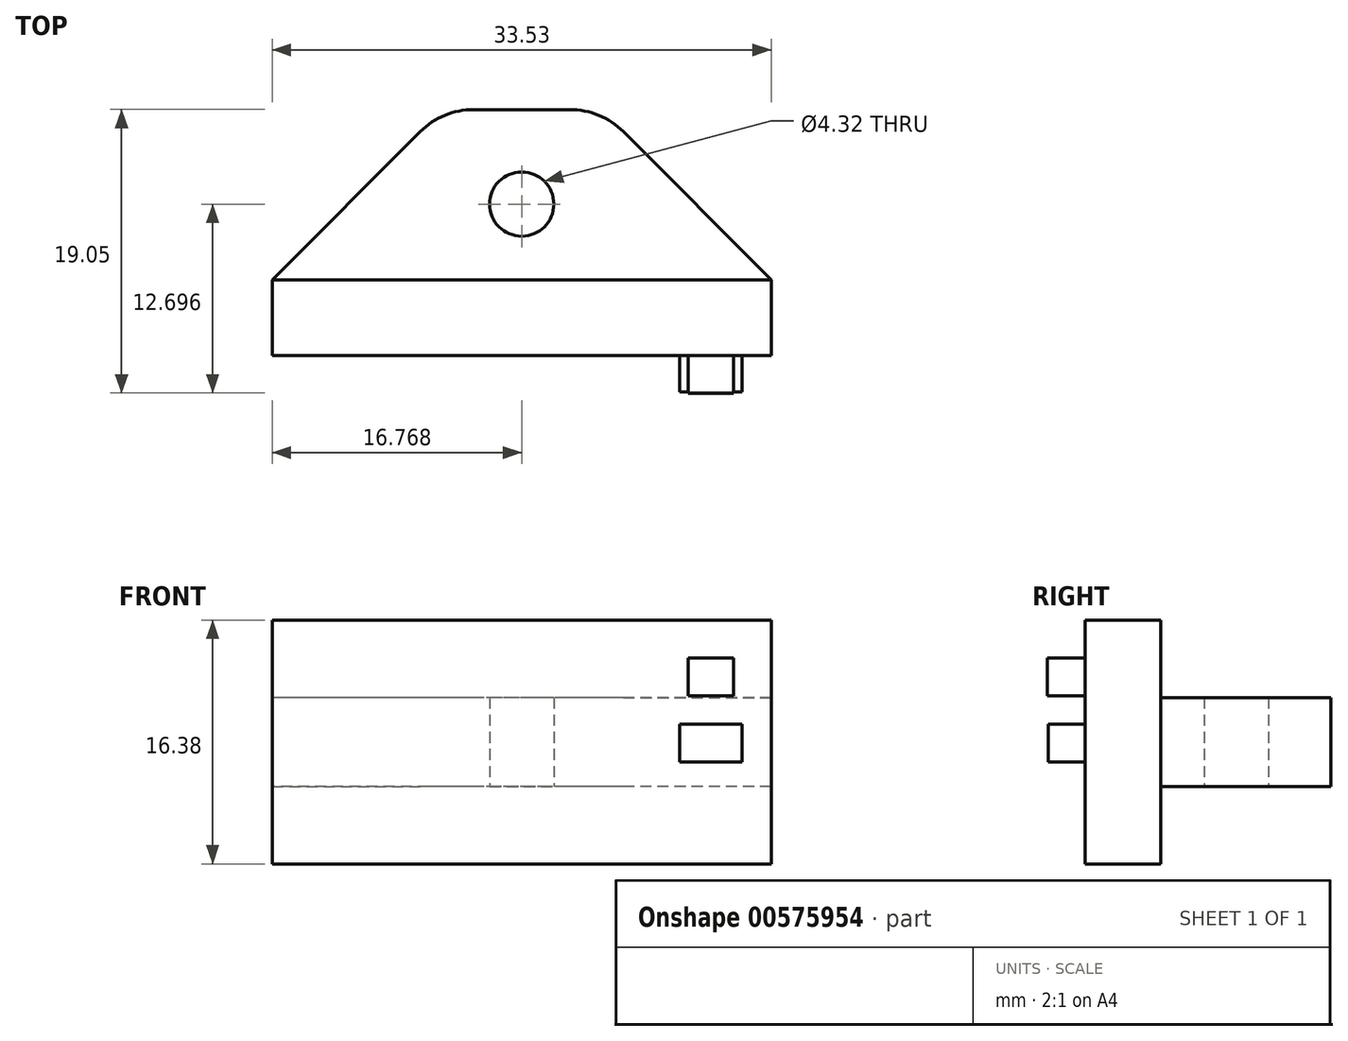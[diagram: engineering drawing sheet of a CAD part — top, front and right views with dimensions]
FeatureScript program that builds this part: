
annotation { "Feature Type Name" : "Feature", "Feature Type Description" : "" }
export const myFeature = defineFeature(function(context is Context, id is Id, definition is map)
    precondition{}
    {
        {
            var Q0;
            Q0=qCreatedBy(makeId("Top.planeOp"),FACE);
            var sketch = newSketch(context, id + "F0", { "sketchPlane" : qUnion([Q0])});
            skLineSegment(sketch, "E0.bottom", {"start": v(-12.43, 11) * mm, "end": v(21.1, 11) * mm});
            skLineSegment(sketch, "E0.top", {"start": v(-12.43, 5.92) * mm, "end": v(21.1, 5.92) * mm});
            skLineSegment(sketch, "E0.left", {"start": v(-12.43, 11) * mm, "end": v(-12.43, 5.92) * mm});
            skLineSegment(sketch, "E0.right", {"start": v(21.1, 11) * mm, "end": v(21.1, 5.92) * mm});
            skSolve(sketch);
        }
        {
            var Q0;
            Q0=makeQuery(id+"F0.imprint","IMPRINT",FACE,{"disambiguationData":[TD([[makeQuery(id+"F0.imprint","IMPRINT",EDGE,{"derivedFrom":sQuery(id+"F0.wireOp",EDGE,"E0.bottom")}),-1.0]])]});
            extrude(context, id + "F1", {"entities" : qUnion([Q0]), "depth" : 16.38 * mm, "offsetDistance" : 25.4 * mm});
        }
        {
            var Q0;
            Q0=makeQuery(id+"F1.opExtrude","SWEPT_FACE",FACE,{"disambiguationData":[OSD([sQuery(id+"F0.wireOp",EDGE,"E0.bottom")])]});
            var sketch = newSketch(context, id + "F2", { "sketchPlane" : qUnion([Q0])});
            skLineSegment(sketch, "E1.bottom", {"start": v(-21.1, 11.18) * mm, "end": v(12.43, 11.18) * mm});
            skLineSegment(sketch, "E1.top", {"start": v(-21.1, 5.2) * mm, "end": v(12.43, 5.2) * mm});
            skLineSegment(sketch, "E1.left", {"start": v(-21.1, 11.18) * mm, "end": v(-21.1, 5.2) * mm});
            skLineSegment(sketch, "E1.right", {"start": v(12.43, 11.18) * mm, "end": v(12.43, 5.2) * mm});
            skSolve(sketch);
        }
        {
            var Q0;
            Q0=makeQuery(id+"F2.imprint","IMPRINT",FACE,{"disambiguationData":[TD([[makeQuery(id+"F2.imprint","IMPRINT",EDGE,{"derivedFrom":sQuery(id+"F2.wireOp",EDGE,"E1.bottom")}),-1.0]])]});
            extrude(context, id + "F3", {"entities" : qUnion([Q0]), "operationType" : NewBodyOperationType.ADD, "depth" : 11.43 * mm, "offsetDistance" : 25.4 * mm});
        }
        {
            var Q0;
            Q0=makeQuery(id+"F3.opExtrude","CAP_EDGE",EDGE,{"disambiguationData":[OSD([sQuery(id+"F2.wireOp",EDGE,"E1.right")])],"isStart":false});
            var Q1;
            Q1=makeQuery(id+"F3.opExtrude","CAP_EDGE",EDGE,{"disambiguationData":[OSD([sQuery(id+"F2.wireOp",EDGE,"E1.left")])],"isStart":false});
            chamfer(context, id + "F4", {"entities" : qUnion([Q0, Q1]), "width" : 11.43 * mm, "tangentPropagation" : true});
        }
        {
            var Q0;
            Q0=makeQuery(id+"F3.opExtrude","SWEPT_FACE",FACE,{"disambiguationData":[OSD([sQuery(id+"F2.wireOp",EDGE,"E1.top")])]});
            var sketch = newSketch(context, id + "F5", { "sketchPlane" : qUnion([Q0])});
            skCircle(sketch, "E2", {"center": v(4.34, -16.08) * mm, "radius": 2.16 * mm});
            skSolve(sketch);
        }
        {
            var Q0;
            Q0=makeQuery(id+"F5.imprint","IMPRINT",FACE,{"disambiguationData":[TD([[makeQuery(id+"F5.imprint","IMPRINT",EDGE,{"derivedFrom":sQuery(id+"F5.wireOp",EDGE,"E2")}),1.0]])]});
            extrude(context, id + "F6", {"entities" : qUnion([Q0]), "operationType" : NewBodyOperationType.REMOVE, "oppositeDirection" : true, "depth" : 25.4 * mm, "offsetDistance" : 25.4 * mm});
        }
        {
            var Q0;
            Q0=makeQuery(id+"F1.opExtrude","SWEPT_FACE",FACE,{"disambiguationData":[OSD([sQuery(id+"F0.wireOp",EDGE,"E0.top")])]});
            var sketch = newSketch(context, id + "F7", { "sketchPlane" : qUnion([Q0])});
            skLineSegment(sketch, "E3.bottom", {"start": v(15.51, 13.84) * mm, "end": v(18.56, 13.84) * mm});
            skLineSegment(sketch, "E3.top", {"start": v(15.51, 11.3) * mm, "end": v(18.56, 11.3) * mm});
            skLineSegment(sketch, "E3.left", {"start": v(15.51, 13.84) * mm, "end": v(15.51, 11.3) * mm});
            skLineSegment(sketch, "E3.right", {"start": v(18.56, 13.84) * mm, "end": v(18.56, 11.3) * mm});
            skSolve(sketch);
        }
        {
            var Q0;
            Q0=makeQuery(id+"F7.imprint","IMPRINT",FACE,{"disambiguationData":[TD([[makeQuery(id+"F7.imprint","IMPRINT",EDGE,{"derivedFrom":sQuery(id+"F7.wireOp",EDGE,"E3.bottom")}),-1.0]])]});
            extrude(context, id + "F8", {"entities" : qUnion([Q0]), "operationType" : NewBodyOperationType.ADD, "depth" : 2.54 * mm, "offsetDistance" : 25.4 * mm});
        }
        {
            var Q0;
            Q0=makeQuery(id+"F1.opExtrude","SWEPT_FACE",FACE,{"disambiguationData":[OSD([sQuery(id+"F0.wireOp",EDGE,"E0.top")])]});
            var sketch = newSketch(context, id + "F9", { "sketchPlane" : qUnion([Q0])});
            skLineSegment(sketch, "E4.bottom", {"start": v(14.94, 9.4) * mm, "end": v(19.13, 9.4) * mm});
            skLineSegment(sketch, "E4.top", {"start": v(14.94, 6.86) * mm, "end": v(19.13, 6.86) * mm});
            skLineSegment(sketch, "E4.left", {"start": v(14.94, 9.4) * mm, "end": v(14.94, 6.86) * mm});
            skLineSegment(sketch, "E4.right", {"start": v(19.13, 9.4) * mm, "end": v(19.13, 6.86) * mm});
            skSolve(sketch);
        }
        {
            var Q0;
            Q0=makeQuery(id+"F9.imprint","IMPRINT",FACE,{"disambiguationData":[TD([[makeQuery(id+"F9.imprint","IMPRINT",EDGE,{"derivedFrom":sQuery(id+"F9.wireOp",EDGE,"E4.bottom")}),-1.0]])]});
            extrude(context, id + "F10", {"entities" : qUnion([Q0]), "operationType" : NewBodyOperationType.ADD, "depth" : 2.46 * mm, "offsetDistance" : 25.4 * mm});
        }
        {
            var Q0;
            {var subQ0=sQuery(id+"F2.wireOp",EDGE,"E1.right");Q0=makeQuery(id+"F4.opChamfer","BLEND_EDGE",EDGE,{"blendedFrom":[makeQuery(id+"F3.opExtrude","CAP_EDGE",EDGE,{"disambiguationData":[OSD([subQ0])],"isStart":false}),makeQuery(id+"F3.opExtrude","CAP_FACE",FACE,{"disambiguationData":[OSD([sQuery(id+"F2.wireOp",EDGE,"E1.bottom"),sQuery(id+"F2.wireOp",EDGE,"E1.top"),sQuery(id+"F2.wireOp",EDGE,"E1.left"),subQ0])],"isStart":false})],"blendedInto":[makeQuery(id+"F3.opExtrude","CAP_FACE",FACE,{"disambiguationData":[OSD([sQuery(id+"F2.wireOp",EDGE,"E1.bottom"),sQuery(id+"F2.wireOp",EDGE,"E1.top"),sQuery(id+"F2.wireOp",EDGE,"E1.left"),subQ0])],"isStart":false})]});}
            var Q1;
            {var subQ0=sQuery(id+"F2.wireOp",EDGE,"E1.left");Q1=makeQuery(id+"F4.opChamfer","BLEND_EDGE",EDGE,{"blendedFrom":[makeQuery(id+"F3.opExtrude","CAP_EDGE",EDGE,{"disambiguationData":[OSD([subQ0])],"isStart":false}),makeQuery(id+"F3.opExtrude","CAP_FACE",FACE,{"disambiguationData":[OSD([sQuery(id+"F2.wireOp",EDGE,"E1.bottom"),sQuery(id+"F2.wireOp",EDGE,"E1.top"),subQ0,sQuery(id+"F2.wireOp",EDGE,"E1.right")])],"isStart":false})],"blendedInto":[makeQuery(id+"F3.opExtrude","CAP_FACE",FACE,{"disambiguationData":[OSD([sQuery(id+"F2.wireOp",EDGE,"E1.bottom"),sQuery(id+"F2.wireOp",EDGE,"E1.top"),subQ0,sQuery(id+"F2.wireOp",EDGE,"E1.right")])],"isStart":false})]});}
            fillet(context, id + "F11", {"entities" : qUnion([Q0, Q1]), "radius" : 5.08 * mm, "tangentPropagation" : true, "allowEdgeOverflow" : false});
        }
    });
